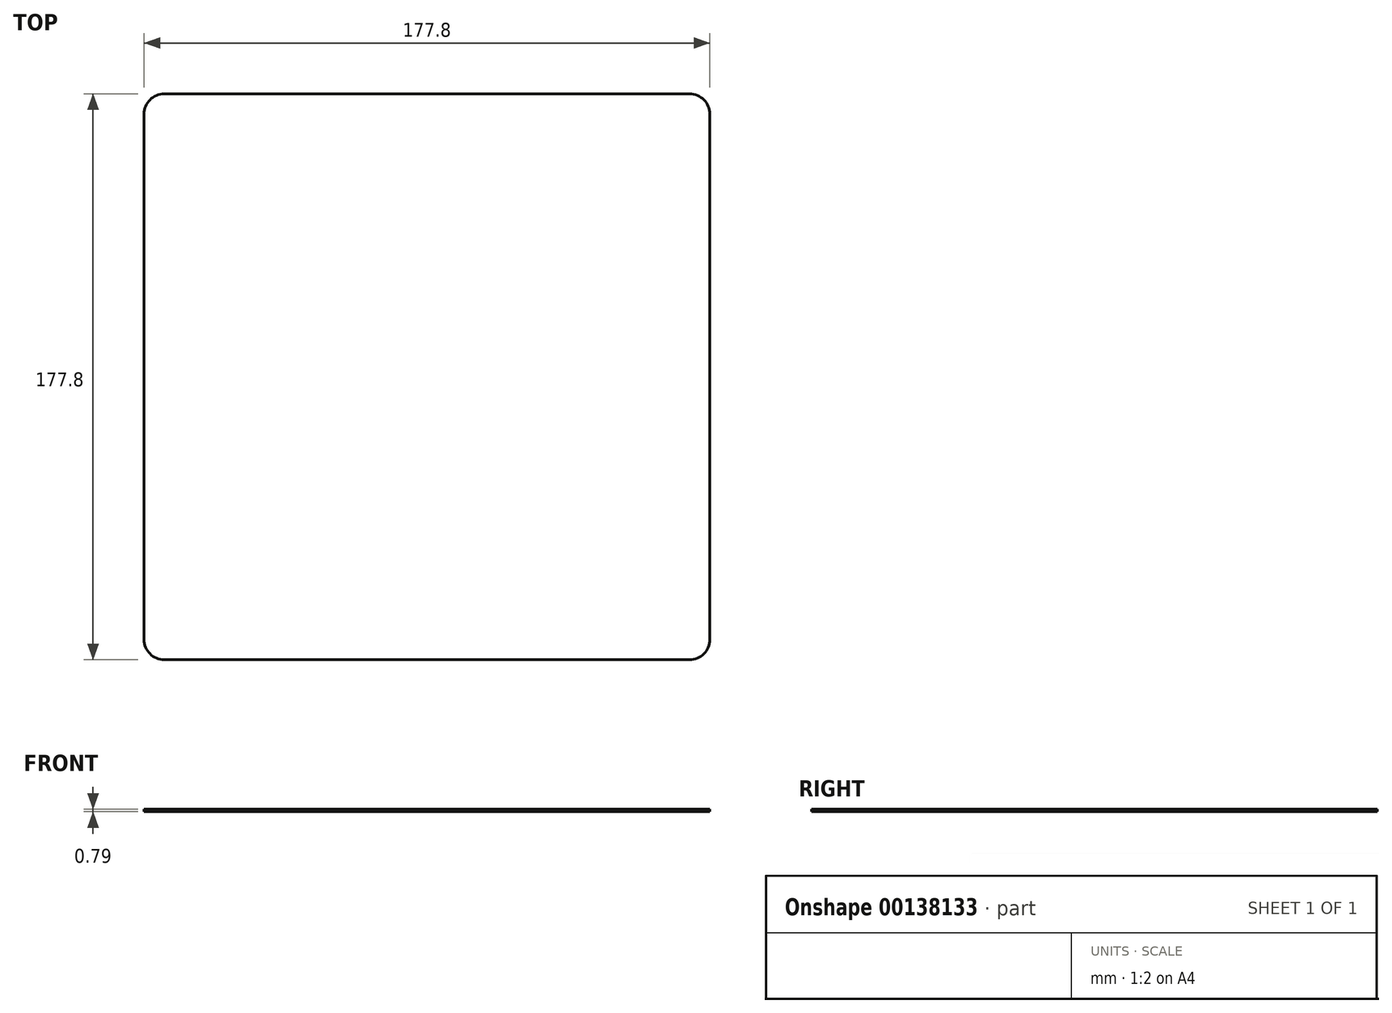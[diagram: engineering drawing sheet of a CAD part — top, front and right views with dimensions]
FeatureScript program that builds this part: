
annotation { "Feature Type Name" : "Feature", "Feature Type Description" : "" }
export const myFeature = defineFeature(function(context is Context, id is Id, definition is map)
    precondition{}
    {
        {
            var Q0;
            Q0=qCreatedBy(makeId("Top.planeOp"),FACE);
            var sketch = newSketch(context, id + "F0", { "sketchPlane" : qUnion([Q0])});
            skLineSegment(sketch, "E0.bottom", {"start": v(0, 0) * mm, "end": v(177.8, 0) * mm});
            skLineSegment(sketch, "E0.top", {"start": v(0, 177.8) * mm, "end": v(177.8, 177.8) * mm});
            skLineSegment(sketch, "E0.left", {"start": v(0, 0) * mm, "end": v(0, 177.8) * mm});
            skLineSegment(sketch, "E0.right", {"start": v(177.8, 0) * mm, "end": v(177.8, 177.8) * mm});
            skSolve(sketch);
        }
        {
            var Q0;
            Q0=makeQuery(id+"F0.imprint","IMPRINT",FACE,{"disambiguationData":[TD([[makeQuery(id+"F0.imprint","IMPRINT",EDGE,{"derivedFrom":sQuery(id+"F0.wireOp",EDGE,"E0.bottom")}),1.0]])]});
            extrude(context, id + "F1", {"entities" : qUnion([Q0]), "depth" : 0.8 * mm});
        }
        {
            var Q0;
            Q0=makeQuery(id+"F1.opExtrude","SWEPT_EDGE",EDGE,{"disambiguationData":[OSD([sQuery(id+"F0.wireOp",EDGE,"E0.top"),sQuery(id+"F0.wireOp",EDGE,"E0.right")])]});
            var Q1;
            Q1=makeQuery(id+"F1.opExtrude","SWEPT_EDGE",EDGE,{"disambiguationData":[OSD([sQuery(id+"F0.wireOp",EDGE,"E0.top"),sQuery(id+"F0.wireOp",EDGE,"E0.left")])]});
            var Q2;
            Q2=makeQuery(id+"F1.opExtrude","SWEPT_EDGE",EDGE,{"disambiguationData":[OSD([sQuery(id+"F0.wireOp",EDGE,"E0.bottom"),sQuery(id+"F0.wireOp",EDGE,"E0.left")])]});
            var Q3;
            Q3=makeQuery(id+"F1.opExtrude","SWEPT_EDGE",EDGE,{"disambiguationData":[OSD([sQuery(id+"F0.wireOp",EDGE,"E0.bottom"),sQuery(id+"F0.wireOp",EDGE,"E0.right")])]});
            fillet(context, id + "F2", {"entities" : qUnion([Q0, Q1, Q2, Q3]), "radius" : 6.35 * mm, "tangentPropagation" : true, "allowEdgeOverflow" : false});
        }
    });
